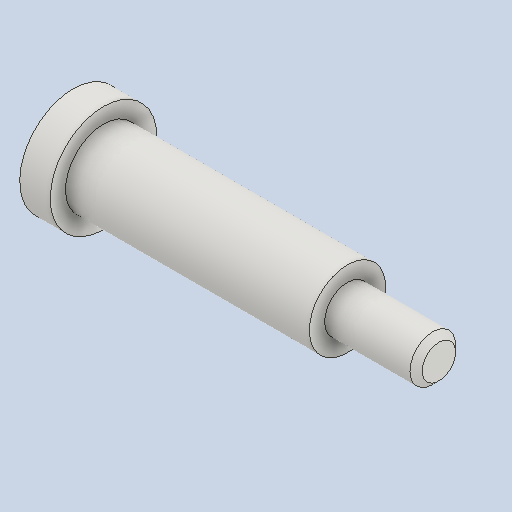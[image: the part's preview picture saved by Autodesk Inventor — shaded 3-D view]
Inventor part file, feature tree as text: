
AUTODESK INVENTOR PART (.ipt)
format: ipt  version: 2022 (Build 260153000, 153)  size: 120,832 bytes
history: native  units: mm
features: other x4, revolve x1, chamfer x1
ambient origin geometry x6: Origin, XZ Plane, XY Plane, X Axis, Y Axis, Z Axis
bodies: Body1 (feature_tree)
feature tree (6):
  other  "Твердое тело1"
  revolve  "Вращение1"
  chamfer  "Фаска1"  [1 undecoded]
  other  "Начальная плоскость"
  other  "Исходная точка"
  other  "Основной эскиз"
note: 1 required parameter value undecoded (feature->parameter linkage not recoverable at this tier; creation-order binding heuristic only, values carry confidence <= 0.55)
